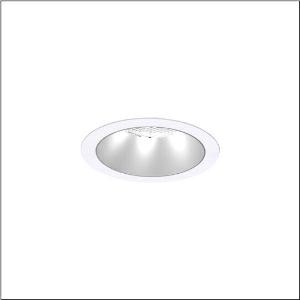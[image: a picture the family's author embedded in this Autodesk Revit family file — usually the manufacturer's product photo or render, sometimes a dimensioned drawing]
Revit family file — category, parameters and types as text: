
# Revit family: lunis_21_l_51db19ed91c
name_source: partatom
category: Lighting Fixtures
units: mm (PartAtom-declared; Revit-internal decimal feet)

## family parameters
Cut with Voids When Loaded = No
Host = Face
Light Source = No
Part Type = Normal
Room Calculation Point = No
Round Connector Dimension = Use Diameter
Shared = No

## types (1)
- --- (1 x LED, 3900 lm, 25.4 W, 4000K)
    Apparent Load = 25 VA
    CIE Flux Codes = 90 99 100 100 100
    Color Rendering = 80
    Color Temperature = 4000K
    Default Elevation = 1800 mm
    Description = Lunis 21,  L, downlight, light control with lens, of PMMA, anti glare with reflector, of PC, matt, light emission: direct distribution, LED rated luminous flux: 2.020lm, light colour: 830/840/865, with terminal, 5-pole, mains connection: 220..240V, AC/DC, 0/50..60Hz, housing, round, of diecast aluminium, traffic white (RAL 9016), diameter: 165mm, clamping range: 1..40mm, protection rating (complete): IP20, protection rating (on room side): IP54, insulation class (complete): insulation class II (safety insulation), certification: CE, impact resistance: IK03, packaging unit: 1 piece
    Height = 0 mm  [stored 0 ft]
    Lamp = 1 x LED
    Lamp Light Flux = 3900 lm
    Lamp Power = 25.4 W
    Lamp count = 1
    Length = 165 mm
    Luminous efficacy = 154 lm/W
    Manufacturer = Siteco
    ModVariant = No
    Model = 51DB19ED91C
    Mounting Place = Ceiling
    Mounting Type = Recessed
    Number of Poles = 1
    OnlyDefault = Yes
    Power Factor = 1
    Product Name = Lunis 21 L
    Product group = downlight
    ProductGroupID = 400
    Protection Class = Protection class II
    Protection Degree = IP 20
    RLX_Detail_Level = 1
    RLX_Emergency_Light_Flux = 0 lm
    RLX_Emergency_Type = 0
    RLX_Emergency_Type_DB = No
    RlxData = <blob elided: 15121 chars, md5=3cc271a9>
    Socket = socket
    Standby Power = 0 W
    System Light Flux = 3900 lm
    System Power = 25 W
    Type Comments = individual setting: colour temperature 4000K, luminous flux: 100 % | (ON | ON | OFF | OFF) | 700 mA
    Type Image = l_1291096.jpg
    URL = http://relux.com
    VarID = @adj_022169
    Voltage = 0 V
    Weight = 0.00 kg
    Width = 0 mm  [stored 0 ft]

note: [stored X ft] marks values corroborated as IEEE doubles in the binary element streams (Revit-internal decimal feet)

## geometry (parser evidence)
native form markers: Sweep x9
no freeform markers — native parametric forms only
